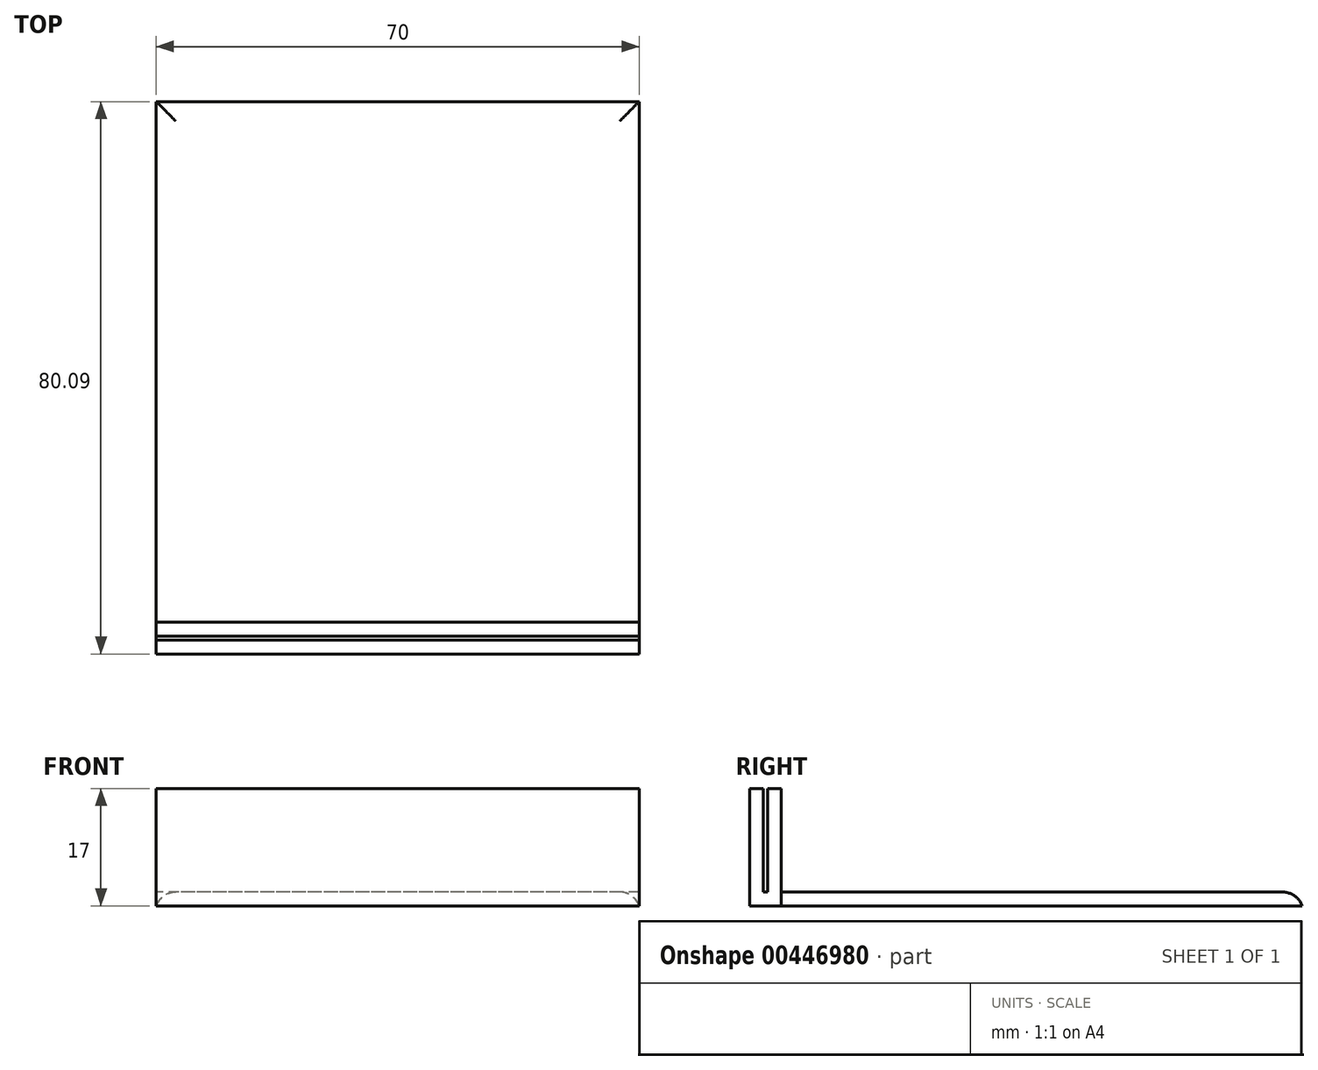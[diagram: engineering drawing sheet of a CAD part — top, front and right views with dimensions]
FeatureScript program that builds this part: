
annotation { "Feature Type Name" : "Feature", "Feature Type Description" : "" }
export const myFeature = defineFeature(function(context is Context, id is Id, definition is map)
    precondition{}
    {
        {
            var Q0;
            Q0=qCreatedBy(makeId("Right.planeOp"),FACE);
            var sketch = newSketch(context, id + "F0", { "sketchPlane" : qUnion([Q0])});
            skLineSegment(sketch, "E0.bottom", {"start": v(-48.82, -2.8) * mm, "end": v(31.18, -2.8) * mm});
            skLineSegment(sketch, "E0.top", {"start": v(-48.82, -4.8) * mm, "end": v(31.18, -4.8) * mm});
            skLineSegment(sketch, "E0.left", {"start": v(-48.82, -2.8) * mm, "end": v(-48.82, -4.8) * mm});
            skLineSegment(sketch, "E0.right", {"start": v(31.18, -2.8) * mm, "end": v(31.18, -4.8) * mm});
            skLineSegment(sketch, "E1.bottom", {"start": v(-48.9, 12.2) * mm, "end": v(-46.9, 12.2) * mm});
            skLineSegment(sketch, "E1.top", {"start": v(-48.9, -4.8) * mm, "end": v(-46.9, -4.8) * mm});
            skLineSegment(sketch, "E1.left", {"start": v(-48.9, 12.2) * mm, "end": v(-48.9, -4.8) * mm});
            skLineSegment(sketch, "E1.right", {"start": v(-46.9, 12.2) * mm, "end": v(-46.9, -4.8) * mm});
            skLineSegment(sketch, "E2.bottom", {"start": v(-46.3, 12.2) * mm, "end": v(-44.3, 12.2) * mm});
            skLineSegment(sketch, "E2.top", {"start": v(-46.3, -4.8) * mm, "end": v(-44.3, -4.8) * mm});
            skLineSegment(sketch, "E2.left", {"start": v(-46.3, 12.2) * mm, "end": v(-46.3, -4.8) * mm});
            skLineSegment(sketch, "E2.right", {"start": v(-44.3, 12.2) * mm, "end": v(-44.3, -4.8) * mm});
            skSolve(sketch);
        }
        {
            var Q0;
            Q0 = qSketchRegion(id + "F0", true);
            extrude(context, id + "F1", {"entities" : qUnion([Q0]), "endBound" : BoundingType.SYMMETRIC, "depth" : 70 * mm});
        }
        {
            var Q0;
            {var subQ0=sQuery(id+"F0.wireOp",EDGE,"E0.bottom");Q0=makeQuery(id+"F1.opExtrude","CAP_EDGE",EDGE,{"disambiguationData":[OSD([subQ0]),TDD([makeQuery(id+"F0.imprint","IMPRINT",EDGE,{"disambiguationData":[TD([[makeQuery(id+"F0.imprint","INTERSECT",VERTEX,{"derivedFrom":[subQ0,sQuery(id+"F0.wireOp",EDGE,"E0.right")]}),1.0]])],"derivedFrom":subQ0})])],"isStart":false});}
            var Q1;
            Q1=makeQuery(id+"F1.opExtrude","SWEPT_EDGE",EDGE,{"disambiguationData":[OSD([sQuery(id+"F0.wireOp",EDGE,"E0.bottom"),sQuery(id+"F0.wireOp",EDGE,"E0.right")])]});
            var Q2;
            {var subQ0=sQuery(id+"F0.wireOp",EDGE,"E0.bottom");Q2=makeQuery(id+"F1.opExtrude","CAP_EDGE",EDGE,{"disambiguationData":[OSD([subQ0]),TDD([makeQuery(id+"F0.imprint","IMPRINT",EDGE,{"disambiguationData":[TD([[makeQuery(id+"F0.imprint","INTERSECT",VERTEX,{"derivedFrom":[subQ0,sQuery(id+"F0.wireOp",EDGE,"E0.right")]}),1.0]])],"derivedFrom":subQ0})])],"isStart":true});}
            fillet(context, id + "F2", {"entities" : qUnion([Q0, Q1, Q2]), "radius" : 3 * mm, "tangentPropagation" : true, "allowEdgeOverflow" : false});
        }
    });
